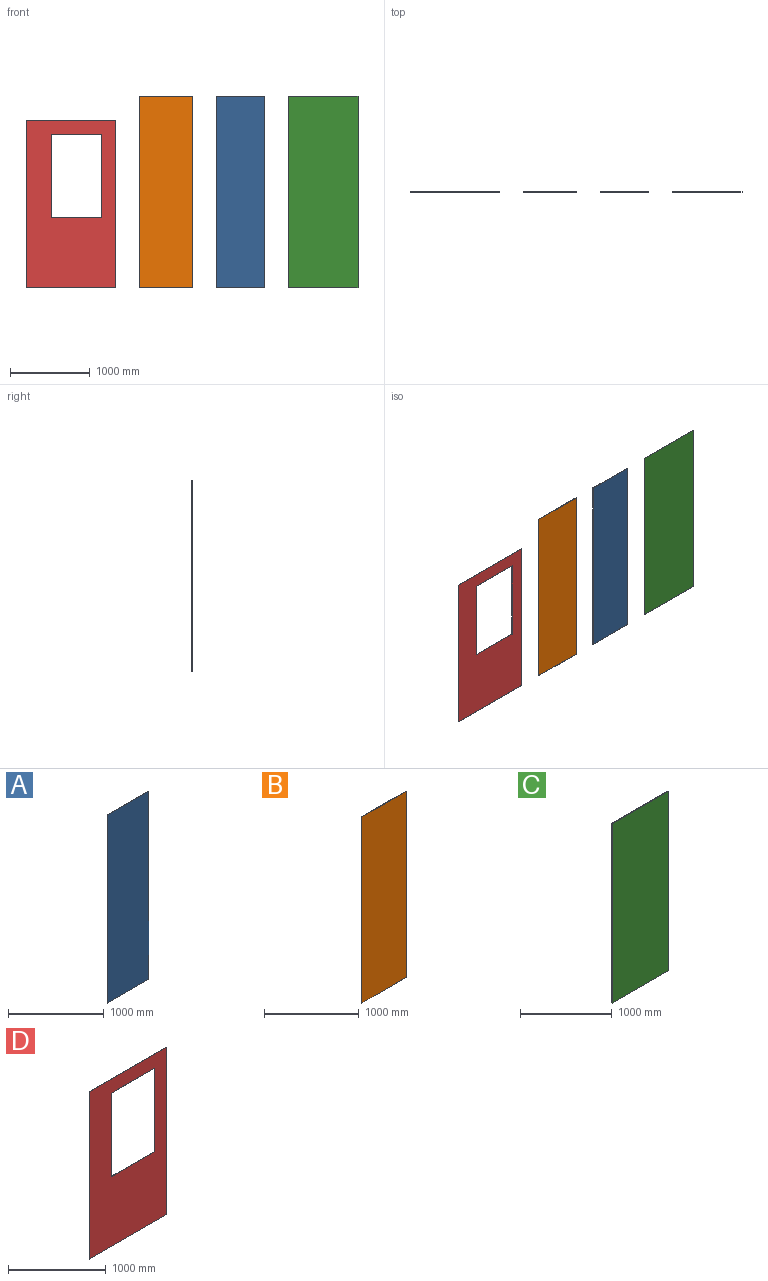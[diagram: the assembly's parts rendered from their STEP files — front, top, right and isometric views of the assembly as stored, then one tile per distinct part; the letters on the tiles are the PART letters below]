
ASSEMBLY  parts=4 mates=3
PART A: 6 faces, bbox 610x5x2400 mm
  f0: plane 2400x5mm, normal (-1,0,0), area 12000mm2, adj f1,f3,f4,f5
  f1: plane 610x5mm, normal (0,0,-1), area 3050mm2, adj f0,f2,f4,f5
  f2: plane 2400x5mm, normal (1,0,0), area 12000mm2, adj f1,f3,f4,f5
  f3: plane 610x5mm, normal (0,0,1), area 3050mm2, adj f0,f2,f4,f5
  f4: plane 2400x610mm, normal (0,-1,0), area 1464000mm2, adj f0,f1,f2,f3
  f5: plane 2400x610mm, normal (0,1,0), area 1464000mm2, adj f0,f1,f2,f3
PART B: 6 faces, bbox 665x5x2400 mm
  f0: plane 2400x5mm, normal (-1,0,0), area 12000mm2, adj f1,f3,f4,f5
  f1: plane 665x5mm, normal (0,0,-1), area 3325mm2, adj f0,f2,f4,f5
  f2: plane 2400x5mm, normal (1,0,0), area 12000mm2, adj f1,f3,f4,f5
  f3: plane 665x5mm, normal (0,0,1), area 3325mm2, adj f0,f2,f4,f5
  f4: plane 2400x665mm, normal (0,-1,0), area 1596000mm2, adj f0,f1,f2,f3
  f5: plane 2400x665mm, normal (0,1,0), area 1596000mm2, adj f0,f1,f2,f3
PART C: 6 faces, bbox 870x5x2400 mm
  f0: plane 2400x5mm, normal (-1,0,0), area 12000mm2, adj f1,f3,f4,f5
  f1: plane 870x5mm, normal (0,0,-1), area 4350mm2, adj f0,f2,f4,f5
  f2: plane 2400x5mm, normal (1,0,0), area 12000mm2, adj f1,f3,f4,f5
  f3: plane 870x5mm, normal (0,0,1), area 4350mm2, adj f0,f2,f4,f5
  f4: plane 2400x870mm, normal (0,-1,0), area 2088000mm2, adj f0,f1,f2,f3
  f5: plane 2400x870mm, normal (0,1,0), area 2088000mm2, adj f0,f1,f2,f3
PART D: 10 faces, bbox 1120x5x2100 mm
  f0: plane 2100x5mm, normal (-1,0,0), area 10500mm2, adj f1,f7,f8,f9
  f1: plane 1120x5mm, normal (0,0,-1), area 5600mm2, adj f0,f2,f8,f9
  f2: plane 2100x5mm, normal (1,0,0), area 10500mm2, adj f1,f7,f8,f9
  f3: plane 630x5mm, normal (0,0,1), area 3150mm2, adj f4,f6,f8,f9
  f4: plane 1050x5mm, normal (1,0,0), area 5250mm2, adj f3,f5,f8,f9
  f5: plane 630x5mm, normal (0,0,-1), area 3150mm2, adj f4,f6,f8,f9
  f6: plane 1050x5mm, normal (-1,0,0), area 5250mm2, adj f3,f5,f8,f9
  f7: plane 1120x5mm, normal (0,0,1), area 5600mm2, adj f0,f2,f8,f9
  f8: plane 2100x1120mm, normal (0,-1,0), area 1690500mm2, adj f0,f1,f2,f3,f4,f5,f6,f7
  f9: plane 2100x1120mm, normal (0,1,0), area 1690500mm2, adj f0,f1,f2,f3,f4,f5,f6,f7
PLACE A at identity
PLACE B t=(-295,0,0)mm
PLACE C t=(200,0,0)mm
PLACE D t=(-590,0,0)mm
MATE fastened D.f8 <-> B.f4  axis (0,-1,0) through (530,-535,235)mm
MATE fastened B.f4 <-> A.f4  axis (0,-1,0) through (1495,-535,235)mm
MATE fastened A.f4 <-> C.f4  axis (0,-1,0) through (2405,-535,235)mm
